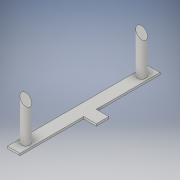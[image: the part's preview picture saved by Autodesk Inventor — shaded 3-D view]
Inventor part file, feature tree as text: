
AUTODESK INVENTOR PART (.ipt)
format: ipt  version: 2018 (Build 220112000, 112)  size: 132,608 bytes
history: native  units: in
note: dims shown in document units (in); Inventor stores cm internally (conversion verified against a paired STEP export)
features: extrude x3, sketch x3
ambient origin geometry x8: Origin, YZ Plane, XZ Plane, XY Plane, X Axis, Y Axis, Z Axis, Center Point
bodies: Solid1 (feature_tree)
feature tree (6):
  extrude  "Extrusion1"  Depth=0.4724in
  extrude  "Extrusion2"  Depth=0.2362in
  extrude  "Extrusion3"  Depth=0.0394in
  sketch  "Sketch1"  dims[d0=0.2362in d1=0.4724in]
  sketch  "Sketch2"  dims[d2=0.1181in d3=0.2362in]
  sketch  "Sketch3"  dims[d4=2.6378in d5=2.1811in d6=1.0906in d7=1.0906in d8=0.1575in d9=0.1575in d10=0.0394in d11=0.0in d12=2.1811in d13=1.0906in d14=1.0906in d15=0.1575in d16=0.1575in d17=0.7874in d18=0.0in d19=0.2756in d20=3.937in d21=0.0in]
